# Revit family: Arper_Aava-02_stool_counter_upholstery_7637
name_source: partatom
category: Furniture
units: mm (PartAtom-declared; Revit-internal decimal feet)

## family parameters
Always vertical = Yes
Cut with Voids When Loaded = No
OmniClass Number = 23.40.20.00
OmniClass Title = General Furniture and Specialties
Room Calculation Point = No
Shared = No
Work Plane-Based = No

## types (1)
- Arper_Aava-02_stool_counter_upholstery_7637
    Default Elevation = 0 mm  [stored 0 ft]
    Description = Stool on a sled base in chromed or powder-coated steel. Shell in 
wood upholstered with fabric, leather, coated fabric or customer’s 
own material. The upholstery can be separated and replaced by 
technical personnel, since it has been applied without the use of 
glue. Glides are also available, with felt insert for wood floors. Seat 
height 66 cm.
    Manufacturer = ARPER s.p.a.
    Model = Aava 02
    URL = http://www.arper.com

note: [stored X ft] marks values corroborated as IEEE doubles in the binary element streams (Revit-internal decimal feet)
